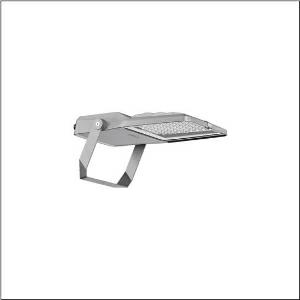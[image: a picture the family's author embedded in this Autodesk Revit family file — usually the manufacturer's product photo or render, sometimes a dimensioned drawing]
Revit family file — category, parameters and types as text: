
# Revit family: floodlight_fl_21_iq_mini___pl52_5xa7772d5d1a_a443
name_source: partatom
category: Lighting Fixtures
units: mm (PartAtom-declared; Revit-internal decimal feet)

## family parameters
Cut with Voids When Loaded = No
Host = Face
Light Source = No
Part Type = Normal
Room Calculation Point = No
Round Connector Dimension = Use Diameter
Shared = No

## types (1)
- --- (1 x LED, 16640 lm, 143 W, 4000K)
    Apparent Load = 143 VA
    CIE Flux Codes = 26 60 98 100 100
    Color Rendering = 80
    Color Temperature = 4000K
    Default Elevation = 1800 mm
    Description = Floodlight FL 21 iQ mini, floodlight, primary light control with lens, of PMMA, primary optical cover: protective disc, of toughened safety glass, transparent, light distribution: PL52, light emission: direct distribution, installation type: surface-mounted, LED, High Power LED, rated luminous flux: 16.640lm, luminous efficacy: 116lm/W, light colour: 840, colour temperature: 4000K, control gear: iQ Street-Remote/DALI, control: Street-Remote, Auto-Match, Temp-Guard, Night-Set, Smart-Wire, Desk-Remote (wireless, voltage-free reading and setting of iQ features in the workshop via application-optimized NFC function/RFID function), optimised constant luminous flux control (CLO 2.0), with terminal, 6-pole, mains connection: 220..240V, AC, 50/60Hz, start of lifetime: 143W, end of service life: 152W, reduction: 61W, luminaire housing, of diecast aluminium, powder-coated, Siteco® metallic grey (DB 702S), corrosivity category C5 mid according to DIN EN ISO 12944, suitable for swimming pools, chlorine-resistant, sealing non-destructively replaceable, mounting bracket, of steel, galvanised, powder-coated, Siteco® metallic grey (DB 702S), protection rating (complete): IP66, insulation class (complete): insulation class II (safety insulation), certification: CE, ENEC, VDE, protection symbol: D, impact resistance: IK08, permissible operating ambient temperature: -40..+40°C, permissible operating ambient temperature for outdoor applications: -40..+50°C, standard: DIN EN 12944, LABS conformity tested according to VDMA 24364:2018-05, packaging unit: 1 piece

Light Distribution: PL52
    Height = 70 mm
    Lamp = 1 x LED
    Lamp Light Flux = 16640 lm
    Lamp Power = 143 W
    Lamp count = 1
    Length = 485 mm
    Luminous efficacy = 116 lm/W
    Manufacturer = Siteco
    ModVariant = No
    Model = 5XA7772D5D1A
    Number of Poles = 1
    OnlyDefault = Yes
    Power Factor = 1
    Product Name = Floodlight FL 21 iQ mini | PL52
    Product group = floodlight | pylon annexe
    ProductGroupID = 6201
    Protection Class = Protection class II
    Protection Degree = IP 66
    RLX_Detail_Level = 1
    RLX_Emergency_Light_Flux = 0 lm
    RLX_Emergency_Type = 0
    RLX_Emergency_Type_DB = No
    RlxData = <blob elided: 96717 chars, md5=ac39e115>
    Socket = socket
    Standby Power = 0 W
    System Light Flux = 16640 lm
    System Power = 143 W
    Type Comments = factory setting: luminous flux: 100 % | dim-lin: 254 | 730 mA
    Type Image = l_1006845.jpg
    URL = http://relux.com
    VarID = @adj_184979
    Voltage = 0 V
    Weight = 0.00 kg
    Width = 337 mm

## geometry (parser evidence)
native form markers: Blend x4, Sweep x13
no freeform markers — native parametric forms only
